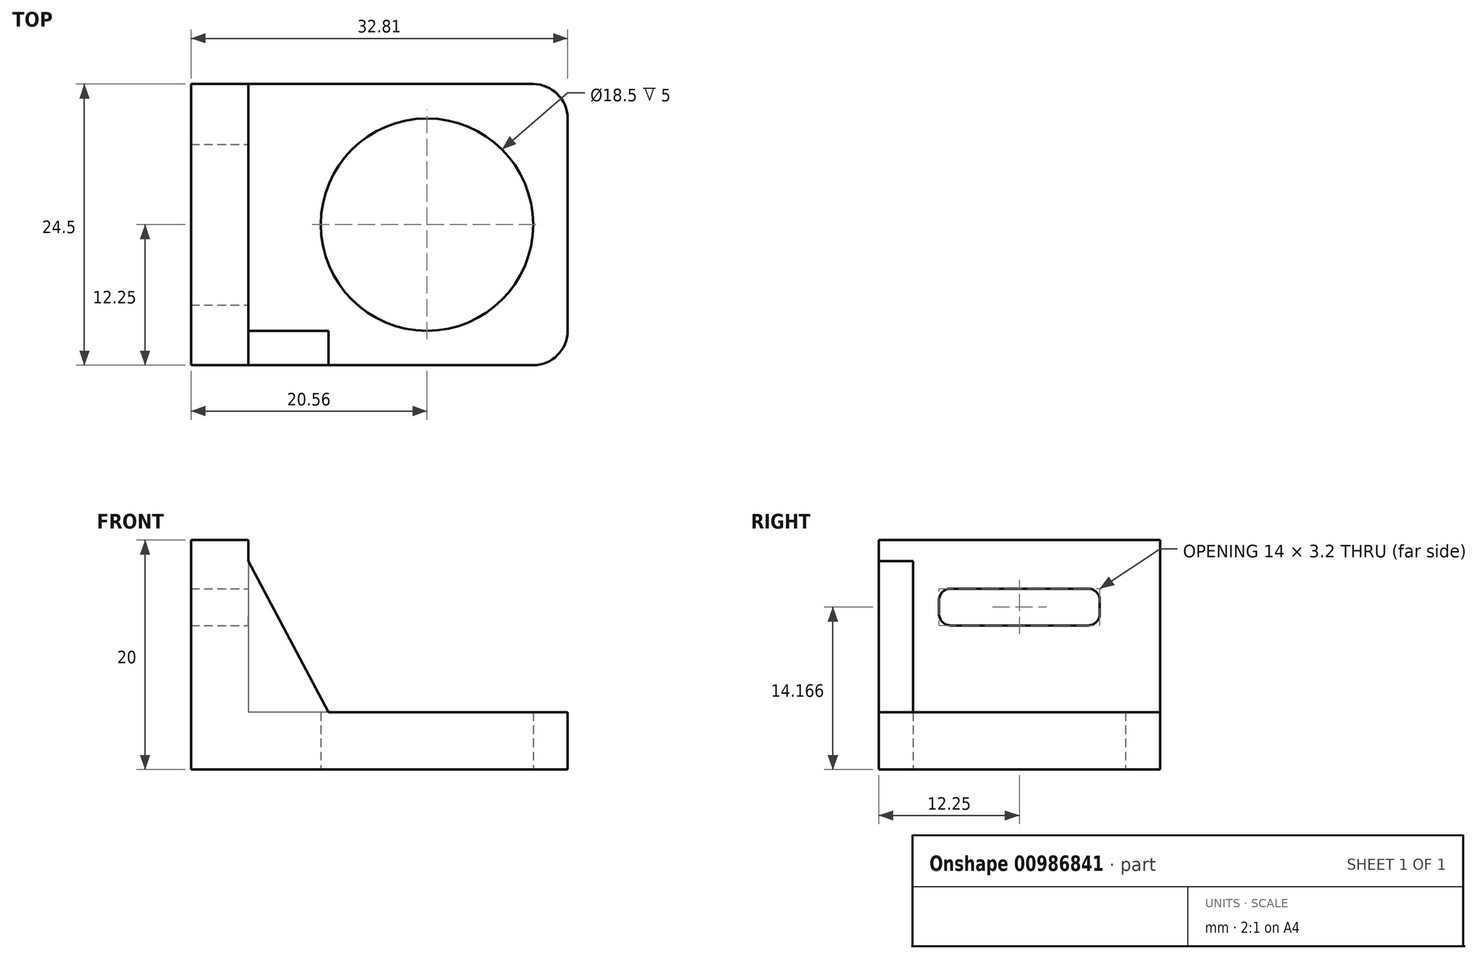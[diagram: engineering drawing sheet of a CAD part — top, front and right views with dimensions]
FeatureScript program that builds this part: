
annotation { "Feature Type Name" : "Feature", "Feature Type Description" : "" }
export const myFeature = defineFeature(function(context is Context, id is Id, definition is map)
    precondition{}
    {
        {
            var Q0;
            Q0=qCreatedBy(makeId("Top.planeOp"),FACE);
            var sketch = newSketch(context, id + "F0", { "sketchPlane" : qUnion([Q0])});
            skLineSegment(sketch, "E0.bottom", {"start": v(12.25, -12.25) * mm, "end": v(-20.56, -12.25) * mm});
            skLineSegment(sketch, "E0.top", {"start": v(12.25, 12.25) * mm, "end": v(-20.56, 12.25) * mm});
            skLineSegment(sketch, "E0.left", {"start": v(12.25, -12.25) * mm, "end": v(12.25, 12.25) * mm});
            skLineSegment(sketch, "E0.right", {"start": v(-20.56, -12.25) * mm, "end": v(-20.56, 12.25) * mm});
            skPoint(sketch, "E0.middle", {"position": v(0, 0) * mm});
            skCircle(sketch, "E1", {"center": v(0, 0) * mm, "radius": 9.25 * mm});
            skSolve(sketch);
        }
        {
            var Q0;
            Q0 = qSketchRegion(id + "F0", true);
            extrude(context, id + "F1", {"entities" : qUnion([Q0]), "depth" : 5 * mm, "offsetDistance" : 25 * mm});
        }
        {
            var Q0;
            Q0=makeQuery(id+"F1.opExtrude","CAP_FACE",FACE,{"disambiguationData":[OSD([sQuery(id+"F0.wireOp",EDGE,"E0.bottom"),sQuery(id+"F0.wireOp",EDGE,"E0.top"),sQuery(id+"F0.wireOp",EDGE,"E0.left"),sQuery(id+"F0.wireOp",EDGE,"E0.right"),sQuery(id+"F0.wireOp",EDGE,"E1")])],"isStart":false});
            var sketch = newSketch(context, id + "F2", { "sketchPlane" : qUnion([Q0])});
            skLineSegment(sketch, "E2.bottom", {"start": v(-20.56, 12.25) * mm, "end": v(-15.56, 12.25) * mm});
            skLineSegment(sketch, "E2.top", {"start": v(-20.56, -12.25) * mm, "end": v(-15.56, -12.25) * mm});
            skLineSegment(sketch, "E2.left", {"start": v(-20.56, 12.25) * mm, "end": v(-20.56, -12.25) * mm});
            skLineSegment(sketch, "E2.right", {"start": v(-15.56, 12.25) * mm, "end": v(-15.56, -12.25) * mm});
            skSolve(sketch);
        }
        {
            var Q0;
            Q0 = qSketchRegion(id + "F2", true);
            extrude(context, id + "F3", {"entities" : qUnion([Q0]), "operationType" : NewBodyOperationType.ADD, "depth" : 15 * mm, "offsetDistance" : 25 * mm});
        }
        {
            var Q0;
            Q0=makeQuery(id+"F3.boolean.opBoolean","MERGE",FACE,{"derivedFrom":[makeQuery(id+"F1.opExtrude","SWEPT_FACE",FACE,{"disambiguationData":[OSD([sQuery(id+"F0.wireOp",EDGE,"E0.bottom")])]}),makeQuery(id+"F3.opExtrude","SWEPT_FACE",FACE,{"disambiguationData":[OSD([sQuery(id+"F2.wireOp",EDGE,"E2.top")])]})]});
            var sketch = newSketch(context, id + "F4", { "sketchPlane" : qUnion([Q0])});
            skLineSegment(sketch, "E3", {"start": v(-15.56, 18.16) * mm, "end": v(-8.6, 5) * mm});
            skLineSegment(sketch, "E4", {"start": v(-8.6, 5) * mm, "end": v(-15.56, 5) * mm});
            skLineSegment(sketch, "E5", {"start": v(-15.56, 5) * mm, "end": v(-15.56, 18.16) * mm});
            skPoint(sketch, "E6", {"position": v(-15.56, 12.5) * mm});
            skSolve(sketch);
        }
        {
            var Q0;
            Q0 = qSketchRegion(id + "F4", true);
            extrude(context, id + "F5", {"entities" : qUnion([Q0]), "operationType" : NewBodyOperationType.ADD, "oppositeDirection" : true, "depth" : 3 * mm, "offsetDistance" : 25 * mm});
        }
        {
            var Q0;
            Q0=makeQuery(id+"F3.opExtrude","SWEPT_FACE",FACE,{"disambiguationData":[OSD([sQuery(id+"F2.wireOp",EDGE,"E2.right")])]});
            var sketch = newSketch(context, id + "F6", { "sketchPlane" : qUnion([Q0])});
            skLineSegment(sketch, "E7.bottom", {"start": v(-7, 15.77) * mm, "end": v(7, 15.77) * mm});
            skLineSegment(sketch, "E7.top", {"start": v(-7, 12.57) * mm, "end": v(7, 12.57) * mm});
            skLineSegment(sketch, "E7.left", {"start": v(-7, 15.77) * mm, "end": v(-7, 12.57) * mm});
            skLineSegment(sketch, "E7.right", {"start": v(7, 15.77) * mm, "end": v(7, 12.57) * mm});
            skPoint(sketch, "E8", {"position": v(0, 15.77) * mm});
            skSolve(sketch);
        }
        {
            var Q0;
            Q0 = qSketchRegion(id + "F6", true);
            extrude(context, id + "F7", {"entities" : qUnion([Q0]), "operationType" : NewBodyOperationType.REMOVE, "oppositeDirection" : true, "depth" : 25 * mm, "offsetDistance" : 25 * mm});
        }
        {
            var Q0;
            Q0=makeQuery(id+"F7.boolean.opBoolean","COPY",EDGE,{"derivedFrom":makeQuery(id+"F7.opExtrude","SWEPT_EDGE",EDGE,{"disambiguationData":[OSD([sQuery(id+"F6.wireOp",EDGE,"E7.top"),sQuery(id+"F6.wireOp",EDGE,"E7.right")])]})});
            var Q1;
            Q1=makeQuery(id+"F7.boolean.opBoolean","COPY",EDGE,{"derivedFrom":makeQuery(id+"F7.opExtrude","SWEPT_EDGE",EDGE,{"disambiguationData":[OSD([sQuery(id+"F6.wireOp",EDGE,"E7.bottom"),sQuery(id+"F6.wireOp",EDGE,"E7.right")])]})});
            var Q2;
            Q2=makeQuery(id+"F7.boolean.opBoolean","COPY",EDGE,{"derivedFrom":makeQuery(id+"F7.opExtrude","SWEPT_EDGE",EDGE,{"disambiguationData":[OSD([sQuery(id+"F6.wireOp",EDGE,"E7.top"),sQuery(id+"F6.wireOp",EDGE,"E7.left")])]})});
            var Q3;
            Q3=makeQuery(id+"F7.boolean.opBoolean","COPY",EDGE,{"derivedFrom":makeQuery(id+"F7.opExtrude","SWEPT_EDGE",EDGE,{"disambiguationData":[OSD([sQuery(id+"F6.wireOp",EDGE,"E7.bottom"),sQuery(id+"F6.wireOp",EDGE,"E7.left")])]})});
            fillet(context, id + "F8", {"entities" : qUnion([Q0, Q1, Q2, Q3]), "radius" : 1 * mm, "tangentPropagation" : true, "allowEdgeOverflow" : false});
        }
        {
            var Q0;
            Q0=makeQuery(id+"F1.opExtrude","SWEPT_EDGE",EDGE,{"disambiguationData":[OSD([sQuery(id+"F0.wireOp",EDGE,"E0.bottom"),sQuery(id+"F0.wireOp",EDGE,"E0.left")])]});
            var Q1;
            Q1=makeQuery(id+"F1.opExtrude","SWEPT_EDGE",EDGE,{"disambiguationData":[OSD([sQuery(id+"F0.wireOp",EDGE,"E0.top"),sQuery(id+"F0.wireOp",EDGE,"E0.left")])]});
            fillet(context, id + "F9", {"entities" : qUnion([Q0, Q1]), "radius" : 3 * mm, "tangentPropagation" : true, "allowEdgeOverflow" : false});
        }
    });
